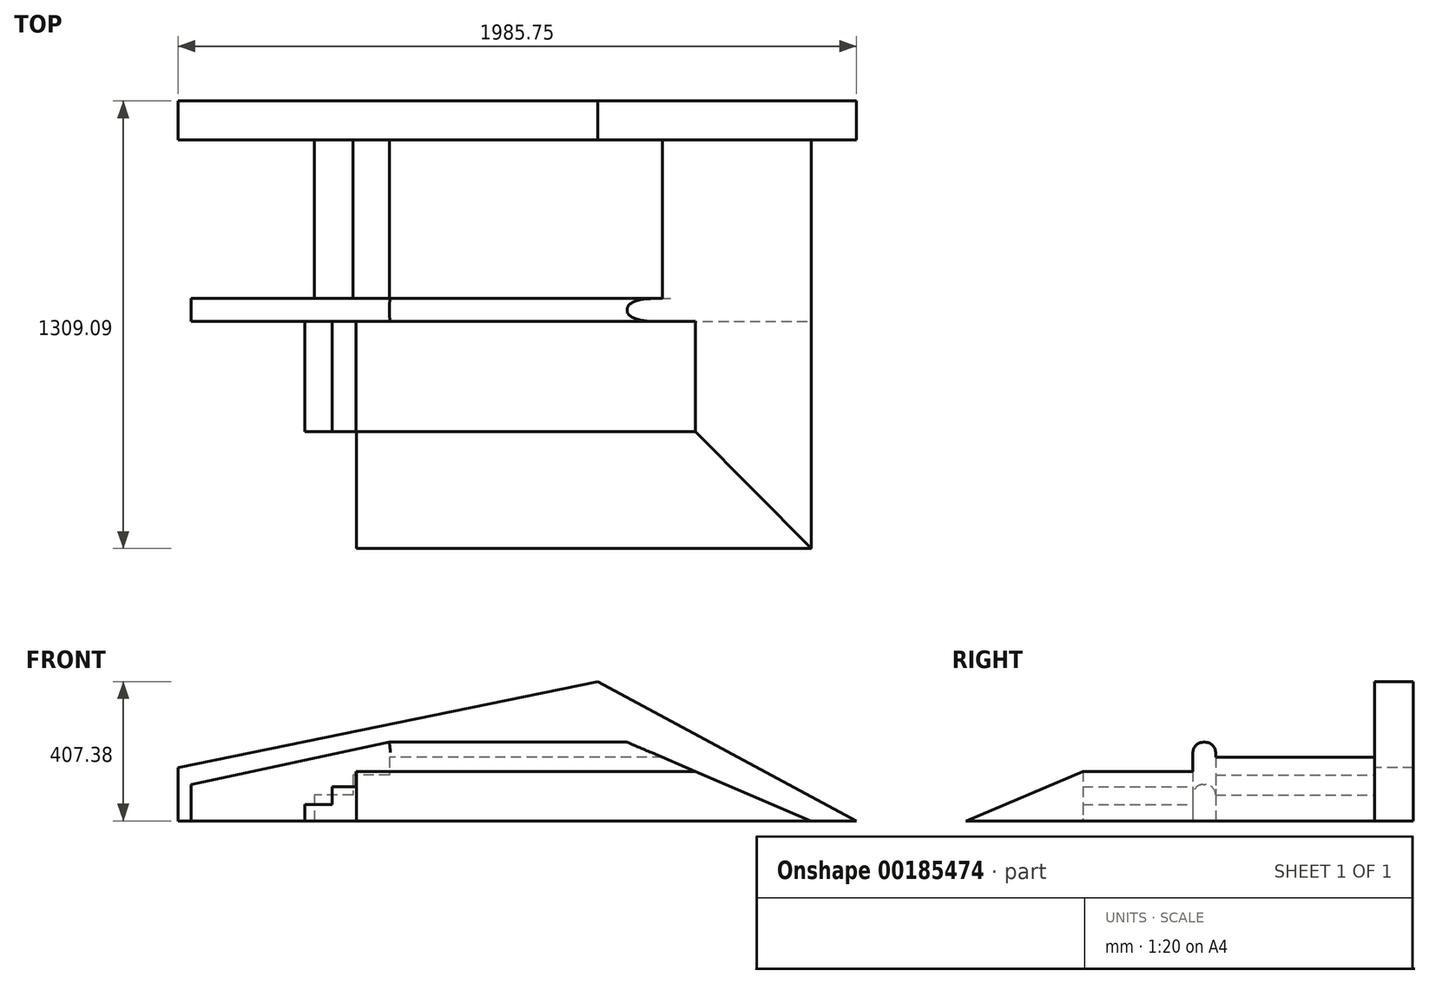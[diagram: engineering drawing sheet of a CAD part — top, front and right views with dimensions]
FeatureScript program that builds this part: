
annotation { "Feature Type Name" : "Feature", "Feature Type Description" : "" }
export const myFeature = defineFeature(function(context is Context, id is Id, definition is map)
    precondition{}
    {
        {
            var Q0;
            Q0=qCreatedBy(makeId("Front.planeOp"),FACE);
            var sketch = newSketch(context, id + "F0", { "sketchPlane" : qUnion([Q0])});
            skLineSegment(sketch, "E0", {"start": v(1070.1, -243.65) * mm, "end": v(312.4, 163.73) * mm});
            skLineSegment(sketch, "E1", {"start": v(312.4, 163.73) * mm, "end": v(-915.65, -88.18) * mm});
            skLineSegment(sketch, "E2", {"start": v(-915.65, -88.18) * mm, "end": v(-915.65, -243.65) * mm});
            skLineSegment(sketch, "E3", {"start": v(-915.65, -243.65) * mm, "end": v(1070.1, -243.65) * mm});
            skSolve(sketch);
        }
        {
            var Q0;
            Q0 = qSketchRegion(id + "F0", true);
            extrude(context, id + "F1", {"entities" : qUnion([Q0]), "oppositeDirection" : true, "depth" : 113.39 * mm});
        }
        {
            var Q0;
            Q0=makeQuery(id+"F1.opExtrude","CAP_FACE",FACE,{"disambiguationData":[OSD([sQuery(id+"F0.wireOp",EDGE,"E0"),sQuery(id+"F0.wireOp",EDGE,"E1"),sQuery(id+"F0.wireOp",EDGE,"E2"),sQuery(id+"F0.wireOp",EDGE,"E3")])],"isStart":true});
            var sketch = newSketch(context, id + "F2", { "sketchPlane" : qUnion([Q0])});
            skLineSegment(sketch, "E4", {"start": v(938.13, -243.65) * mm, "end": v(502.84, -57.7) * mm});
            skLineSegment(sketch, "E5", {"start": v(502.84, -57.7) * mm, "end": v(-296.8, -57.7) * mm});
            skLineSegment(sketch, "E6", {"start": v(-296.8, -57.7) * mm, "end": v(-296.8, -109.29) * mm});
            skLineSegment(sketch, "E7", {"start": v(-296.8, -109.29) * mm, "end": v(-403.2, -109.29) * mm});
            skLineSegment(sketch, "E8", {"start": v(-403.2, -109.29) * mm, "end": v(-403.2, -167.32) * mm});
            skLineSegment(sketch, "E9", {"start": v(-403.2, -167.32) * mm, "end": v(-516.05, -167.32) * mm});
            skLineSegment(sketch, "E10", {"start": v(-516.05, -167.32) * mm, "end": v(-516.05, -243.65) * mm});
            skSolve(sketch);
        }
        {
            var Q0;
            {var subQ0=sQuery(id+"F2.wireOp",EDGE,"E4");Q0=makeQuery(id+"F2.imprint","IMPRINT",FACE,{"disambiguationData":[TD([[makeQuery(id+"F2.imprint","IMPRINT",EDGE,{"derivedFrom":subQ0}),1.0]])]});}
            extrude(context, id + "F3", {"entities" : qUnion([Q0]), "operationType" : NewBodyOperationType.ADD, "depth" : 464.73 * mm});
        }
        {
            var Q0;
            Q0=makeQuery(id+"F3.opExtrude","CAP_FACE",FACE,{"disambiguationData":[OSD([sQuery(id+"F0.wireOp",EDGE,"E3"),sQuery(id+"F2.wireOp",EDGE,"E4"),sQuery(id+"F2.wireOp",EDGE,"E5"),sQuery(id+"F2.wireOp",EDGE,"E6"),sQuery(id+"F2.wireOp",EDGE,"E7"),sQuery(id+"F2.wireOp",EDGE,"E8"),sQuery(id+"F2.wireOp",EDGE,"E9"),sQuery(id+"F2.wireOp",EDGE,"E10")])],"isStart":false});
            var sketch = newSketch(context, id + "F4", { "sketchPlane" : qUnion([Q0])});
            skLineSegment(sketch, "E11", {"start": v(938.13, -243.65) * mm, "end": v(398.8, -13.24) * mm});
            skLineSegment(sketch, "E12", {"start": v(398.8, -13.24) * mm, "end": v(-296.8, -13.24) * mm});
            skLineSegment(sketch, "E13", {"start": v(-296.8, -13.24) * mm, "end": v(-877.53, -136.83) * mm});
            skLineSegment(sketch, "E14", {"start": v(-877.53, -136.83) * mm, "end": v(-877.53, -243.4) * mm});
            skLineSegment(sketch, "E15", {"start": v(-877.53, -243.4) * mm, "end": v(528.2, -243.65) * mm});
            skLineSegment(sketch, "E16", {"start": v(528.2, -243.65) * mm, "end": v(938.13, -243.65) * mm});
            skSolve(sketch);
        }
        {
            var Q0;
            Q0 = qSketchRegion(id + "F4", true);
            extrude(context, id + "F5", {"entities" : qUnion([Q0]), "operationType" : NewBodyOperationType.ADD, "depth" : 66.46 * mm});
        }
        {
            var Q0;
            Q0=makeQuery(id+"F5.opExtrude","CAP_EDGE",EDGE,{"disambiguationData":[OSD([sQuery(id+"F4.wireOp",EDGE,"E12")])],"isStart":true});
            var Q1;
            Q1=makeQuery(id+"F5.opExtrude","CAP_EDGE",EDGE,{"disambiguationData":[OSD([sQuery(id+"F4.wireOp",EDGE,"E12")])],"isStart":false});
            var Q2;
            Q2=makeQuery(id+"F5.opExtrude","CAP_EDGE",EDGE,{"disambiguationData":[OSD([sQuery(id+"F4.wireOp",EDGE,"E13")])],"isStart":false});
            var Q3;
            Q3=makeQuery(id+"F5.opExtrude","CAP_EDGE",EDGE,{"disambiguationData":[OSD([sQuery(id+"F4.wireOp",EDGE,"E13")])],"isStart":true});
            fillet(context, id + "F6", {"entities" : qUnion([Q0, Q1, Q2, Q3]), "radius" : 30.48 * mm, "tangentPropagation" : true, "allowEdgeOverflow" : false});
        }
        {
            var Q0;
            Q0=makeQuery(id+"F5.opExtrude","CAP_FACE",FACE,{"disambiguationData":[OSD([sQuery(id+"F4.wireOp",EDGE,"E11"),sQuery(id+"F4.wireOp",EDGE,"E12"),sQuery(id+"F4.wireOp",EDGE,"E13"),sQuery(id+"F4.wireOp",EDGE,"E14"),sQuery(id+"F4.wireOp",EDGE,"E15"),sQuery(id+"F4.wireOp",EDGE,"E16")])],"isStart":false});
            var sketch = newSketch(context, id + "F7", { "sketchPlane" : qUnion([Q0])});
            skLineSegment(sketch, "E17", {"start": v(938.13, -243.65) * mm, "end": v(598.4, -98.52) * mm});
            skLineSegment(sketch, "E18", {"start": v(598.4, -98.52) * mm, "end": v(-393.8, -98.52) * mm});
            skLineSegment(sketch, "E19", {"start": v(-393.8, -98.52) * mm, "end": v(-393.8, -143.11) * mm});
            skLineSegment(sketch, "E20", {"start": v(-393.8, -143.11) * mm, "end": v(-464.7, -143.11) * mm});
            skLineSegment(sketch, "E21", {"start": v(-464.7, -143.11) * mm, "end": v(-464.7, -195.78) * mm});
            skLineSegment(sketch, "E22", {"start": v(-464.7, -195.78) * mm, "end": v(-543.69, -195.78) * mm});
            skLineSegment(sketch, "E23", {"start": v(-543.69, -195.78) * mm, "end": v(-543.69, -243.47) * mm});
            skLineSegment(sketch, "E24", {"start": v(-543.69, -243.47) * mm, "end": v(938.13, -243.65) * mm});
            skSolve(sketch);
        }
        {
            var Q0;
            Q0 = qSketchRegion(id + "F7", true);
            extrude(context, id + "F8", {"entities" : qUnion([Q0]), "operationType" : NewBodyOperationType.ADD, "depth" : 322.3 * mm});
        }
        {
            var Q0;
            Q0=makeQuery(id+"F8.opExtrude","CAP_FACE",FACE,{"disambiguationData":[OSD([sQuery(id+"F7.wireOp",EDGE,"E17"),sQuery(id+"F7.wireOp",EDGE,"E18"),sQuery(id+"F7.wireOp",EDGE,"E19"),sQuery(id+"F7.wireOp",EDGE,"E20"),sQuery(id+"F7.wireOp",EDGE,"E21"),sQuery(id+"F7.wireOp",EDGE,"E22"),sQuery(id+"F7.wireOp",EDGE,"E23"),sQuery(id+"F7.wireOp",EDGE,"E24")])],"isStart":false});
            var sketch = newSketch(context, id + "F9", { "sketchPlane" : qUnion([Q0])});
            skLineSegment(sketch, "E25", {"start": v(598.4, -98.52) * mm, "end": v(598.4, -243.61) * mm});
            skLineSegment(sketch, "E26", {"start": v(598.4, -243.61) * mm, "end": v(938.13, -243.65) * mm});
            skLineSegment(sketch, "E27", {"start": v(938.13, -243.65) * mm, "end": v(598.4, -98.52) * mm});
            skSolve(sketch);
        }
        {
            var Q0;
            Q0 = qSketchRegion(id + "F9", true);
            extrude(context, id + "F10", {"entities" : qUnion([Q0]), "operationType" : NewBodyOperationType.ADD, "depth" : 342.2 * mm});
        }
        {
            var Q0;
            Q0=makeQuery(id+"F10.opExtrude","SWEPT_FACE",FACE,{"disambiguationData":[OSD([sQuery(id+"F9.wireOp",EDGE,"E25")])]});
            var sketch = newSketch(context, id + "F11", { "sketchPlane" : qUnion([Q0])});
            skLineSegment(sketch, "E28", {"start": v(853.5, -243.61) * mm, "end": v(853.5, -98.52) * mm});
            skLineSegment(sketch, "E29", {"start": v(853.5, -98.52) * mm, "end": v(1195.7, -243.61) * mm});
            skLineSegment(sketch, "E30", {"start": v(1195.7, -243.61) * mm, "end": v(853.5, -243.61) * mm});
            skSolve(sketch);
        }
        {
            var Q0;
            Q0 = qSketchRegion(id + "F11", true);
            extrude(context, id + "F12", {"entities" : qUnion([Q0]), "operationType" : NewBodyOperationType.ADD, "depth" : 991.17 * mm});
        }
        {
            var Q0;
            Q0=makeQuery(id+"F10.opExtrude","SWEPT_EDGE",EDGE,{"disambiguationData":[OSD([sQuery(id+"F7.wireOp",EDGE,"E18"),sQuery(id+"F9.wireOp",EDGE,"E25"),sQuery(id+"F9.wireOp",EDGE,"E27")])]});
            chamfer(context, id + "F13", {"entities" : qUnion([Q0]), "chamferType" : ChamferType.TWO_OFFSETS, "width1" : 254 * mm, "oppositeDirection" : false, "width2" : 368.3 * mm, "tangentPropagation" : true});
        }
    });
